# Revit family: LRTA
name_source: partatom
category: Lighting Fixtures
units: mm (PartAtom-declared; Revit-internal decimal feet)

## family parameters
Always vertical = Yes
Cut with Voids When Loaded = No
Host = Ceiling
Light Source = Yes
OmniClass Number = 23.80.70.11.14.17
OmniClass Title = Direct/Indirect
Part Type = Normal
Room Calculation Point = No
Round Connector Dimension = Use Diameter
Shared = No

## types (13) — shared parameters
Assembly Code = D5020200
Color Filter = 16777215
Description = LED Recessed Type A
Dimming Lamp Color Temperature Shift = <None>
Emit Shape Visible in Rendering = No
Housing Finish = Metal - Viscor - White
Lamp = LED
Lens Finish = Acrylic - Viscor - Frosted Prismatic P12
Manufacturer = VISIONEERING by VISCOR
Model = LRTA
Tilt Angle = 90.00°
URL = https://www.viscor.com
Voltage = 120 V

## per-type parameters (varying)
| type | Apparent Load | Emit from Rectangle Length | Emit from Rectangle Width | Lamp Wattage | Length | Photometric Web File | Width |
| LRTA1x4-LED840K035LUNV | 30 VA | 3' - 11 3/4" | 0' - 11 3/4" | 30 VA | 3' - 11 3/4" | LRTA1x4-LED840K035LUNV-G000911.IES | 0' - 11 3/4" |
| LRTA1x4-LED840K046LUNV | 35 VA | 3' - 11 3/4" | 0' - 11 3/4" | 35 VA | 3' - 11 3/4" | LRTA1x4-LED840K046LUNV-G000915.IES | 0' - 11 3/4" |
| LRTA2X2-LED840K026LUNV | 21 VA | 1' - 11 3/4" | 1' - 11 3/4" | 21 VA | 1' - 11 3/4" | LRTA2X2-LED840K026LUNV-G002041.IES | 1' - 11 3/4" |
| LRTA2x2-LED840K035LUNV | 30 VA | 1' - 11 3/4" | 1' - 11 3/4" | 30 VA | 1' - 11 3/4" | LRTA2x2-LED840K035LUNV-G000879.IES | 1' - 11 3/4" |
| LRTA2x2-LED840K040LUNV | 33 VA | 1' - 11 3/4" | 1' - 11 3/4" | 33 VA | 1' - 11 3/4" | LRTA2X2-LED840K040LUNV-G002033.IES | 1' - 11 3/4" |
| LRTA2x2-LED840K046LUNV | 38 VA | 1' - 11 3/4" | 1' - 11 3/4" | 38 VA | 1' - 11 3/4" | LRTA2x2-LED840K046LUNV-G000935.IES | 1' - 11 3/4" |
| LRTA2x4-LED840K040LUNV | 31 VA | 3' - 11 3/4" | 1' - 11 3/4" | 31 VA | 3' - 11 3/4" | LRTA2x4-LED840K040LUNV-G0897.IES | 1' - 11 3/4" |
| LRTA2x4-LED840K049LUNV | 39 VA | 3' - 11 3/4" | 1' - 11 3/4" | 39 VA | 3' - 11 3/4" | LRTA2x4-LED840K049LUNV-G000895.IES | 1' - 11 3/4" |
| LRTA2x4-LED840K063LUNV | 49 VA | 3' - 11 3/4" | 1' - 11 3/4" | 49 VA | 3' - 11 3/4" | LRTA2x4-LED840K063LUNV-G000926.IES | 1' - 11 3/4" |
| LRTA2x4-LED840K077LUNV | 60 VA | 3' - 11 3/4" | 1' - 11 3/4" | 60 VA | 3' - 11 3/4" | LRTA2x4-LED840K077LUNV-G000902.IES | 1' - 11 3/4" |
| LRTA2x4-LED840K090LUNV | 73 VA | 3' - 11 3/4" | 1' - 11 3/4" | 73 VA | 3' - 11 3/4" | LRTA2x4-LED840K090LUNV-G000906.IES | 1' - 11 3/4" |
| LRTA20x60-LED840K049LUNV-P13 | 35 VA | 4' - 11 3/4" | 1' - 7 3/4" | 35 VA | 4' - 11 3/4" | LRTA20x60-LED840K049LUNV-P13.IES | 1' - 7 3/4" |
| LRTA30x30-LED840K040LUNV-A1 | 37 VA | 2' - 5 3/4" | 2' - 5 3/4" | 37 VA | 2' - 5 3/4" | LRTA30x30-LED840K040LUNV-A1-G001156.IES | 2' - 5 3/4" |

## geometry (parser evidence)
native form markers: Sweep x2
no freeform markers — native parametric forms only
